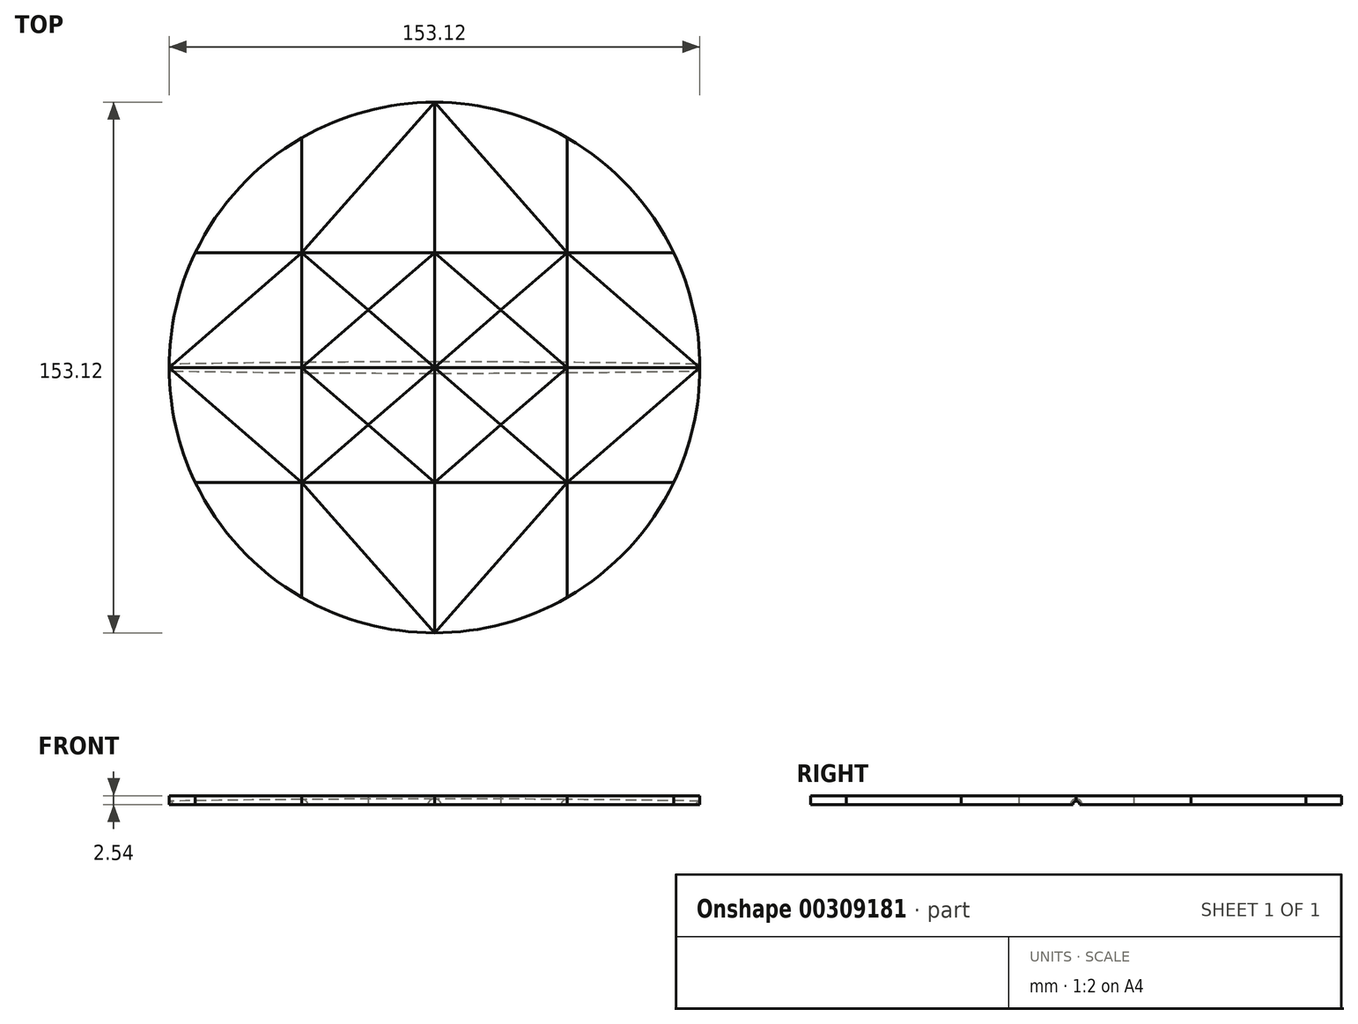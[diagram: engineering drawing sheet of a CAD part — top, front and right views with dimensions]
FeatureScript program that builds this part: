
annotation { "Feature Type Name" : "Feature", "Feature Type Description" : "" }
export const myFeature = defineFeature(function(context is Context, id is Id, definition is map)
    precondition{}
    {
        {
            var Q0;
            Q0=qCreatedBy(makeId("Top.planeOp"),FACE);
            var sketch = newSketch(context, id + "F0", { "sketchPlane" : qUnion([Q0])});
            skCircle(sketch, "E0", {"center": v(0, 0) * mm, "radius": 76.56 * mm});
            skLineSegment(sketch, "E1", {"start": v(0, 0) * mm, "end": v(-76.56, 0) * mm});
            skLineSegment(sketch, "E2", {"start": v(0, 0) * mm, "end": v(0, 76.56) * mm});
            skLineSegment(sketch, "E3", {"start": v(0, 0) * mm, "end": v(76.56, 0) * mm});
            skLineSegment(sketch, "E4", {"start": v(0, 0) * mm, "end": v(0, -76.56) * mm});
            skLineSegment(sketch, "E5", {"start": v(-38.28, 0) * mm, "end": v(-38.28, 66.3) * mm});
            skLineSegment(sketch, "E6", {"start": v(-38.28, 0) * mm, "end": v(-38.28, -66.3) * mm});
            skLineSegment(sketch, "E7", {"start": v(38.28, 0) * mm, "end": v(38.28, 66.3) * mm});
            skLineSegment(sketch, "E8", {"start": v(38.28, 0) * mm, "end": v(38.28, -66.3) * mm});
            skLineSegment(sketch, "E9", {"start": v(-38.28, 33.15) * mm, "end": v(-69, 33.15) * mm});
            skLineSegment(sketch, "E10", {"start": v(-38.28, -33.15) * mm, "end": v(-69, -33.15) * mm});
            skLineSegment(sketch, "E11", {"start": v(38.28, 33.15) * mm, "end": v(69, 33.15) * mm});
            skLineSegment(sketch, "E12", {"start": v(38.28, -33.15) * mm, "end": v(69, -33.15) * mm});
            skLineSegment(sketch, "E13", {"start": v(38.28, -33.15) * mm, "end": v(0, -33.15) * mm});
            skPoint(sketch, "E13.endSnap0", {"position": v(0, -38.28) * mm});
            skLineSegment(sketch, "E14", {"start": v(0, -33.15) * mm, "end": v(-38.28, -33.15) * mm});
            skLineSegment(sketch, "E15", {"start": v(-38.28, 33.15) * mm, "end": v(0, 33.15) * mm});
            skLineSegment(sketch, "E16", {"start": v(0, 33.15) * mm, "end": v(38.28, 33.15) * mm});
            skLineSegment(sketch, "E17", {"start": v(0, 33.15) * mm, "end": v(-38.28, 0) * mm});
            skLineSegment(sketch, "E18", {"start": v(-38.28, 0) * mm, "end": v(0, -33.15) * mm});
            skLineSegment(sketch, "E19", {"start": v(0, -33.15) * mm, "end": v(38.28, 0) * mm});
            skLineSegment(sketch, "E20", {"start": v(38.28, 0) * mm, "end": v(0, 33.15) * mm});
            skLineSegment(sketch, "E21", {"start": v(38.28, 33.15) * mm, "end": v(76.56, 0) * mm});
            skLineSegment(sketch, "E22", {"start": v(76.56, 0) * mm, "end": v(38.28, -33.15) * mm});
            skLineSegment(sketch, "E23", {"start": v(-38.28, 33.15) * mm, "end": v(-76.56, 0) * mm});
            skLineSegment(sketch, "E24", {"start": v(-76.56, 0) * mm, "end": v(-38.28, -33.15) * mm});
            skLineSegment(sketch, "E25", {"start": v(-38.28, -33.15) * mm, "end": v(0, -76.56) * mm});
            skLineSegment(sketch, "E26", {"start": v(0, -76.56) * mm, "end": v(38.28, -33.15) * mm});
            skLineSegment(sketch, "E27", {"start": v(38.28, 33.15) * mm, "end": v(0, 76.56) * mm});
            skLineSegment(sketch, "E28", {"start": v(0, 76.56) * mm, "end": v(-38.28, 33.15) * mm});
            skLineSegment(sketch, "E29", {"start": v(-38.28, 33.15) * mm, "end": v(38.28, -33.15) * mm});
            skLineSegment(sketch, "E30", {"start": v(38.28, 33.15) * mm, "end": v(-38.28, -33.15) * mm});
            skSolve(sketch);
        }
        {
            var Q0;
            {var subQ0=sQuery(id+"F0.wireOp",EDGE,"E28");Q0=makeQuery(id+"F0.imprint","IMPRINT",FACE,{"disambiguationData":[TD([[makeQuery(id+"F0.imprint","IMPRINT",EDGE,{"derivedFrom":subQ0}),-1.0]])]});}
            extrude(context, id + "F1", {"entities" : qUnion([Q0]), "depth" : 2.54 * mm});
        }
        {
            var Q0;
            {var subQ3=sQuery(id+"F0.wireOp",EDGE,"E9");Q0=makeQuery(id+"F0.imprint","IMPRINT",FACE,{"disambiguationData":[TD([[makeQuery(id+"F0.imprint","IMPRINT",EDGE,{"derivedFrom":subQ3}),-1.0]])]});}
            extrude(context, id + "F2", {"entities" : qUnion([Q0]), "depth" : 2.54 * mm});
        }
        {
            var Q0;
            {var subQ2=sQuery(id+"F0.wireOp",EDGE,"E9");Q0=makeQuery(id+"F0.imprint","IMPRINT",FACE,{"disambiguationData":[TD([[makeQuery(id+"F0.imprint","IMPRINT",EDGE,{"derivedFrom":subQ2}),1.0]])]});}
            extrude(context, id + "F3", {"entities" : qUnion([Q0]), "depth" : 2.54 * mm});
        }
        {
            var Q0;
            {var subQ2=sQuery(id+"F0.wireOp",EDGE,"E10");Q0=makeQuery(id+"F0.imprint","IMPRINT",FACE,{"disambiguationData":[TD([[makeQuery(id+"F0.imprint","IMPRINT",EDGE,{"derivedFrom":subQ2}),-1.0]])]});}
            extrude(context, id + "F4", {"entities" : qUnion([Q0]), "depth" : 2.54 * mm});
        }
        {
            var Q0;
            {var subQ3=sQuery(id+"F0.wireOp",EDGE,"E10");Q0=makeQuery(id+"F0.imprint","IMPRINT",FACE,{"disambiguationData":[TD([[makeQuery(id+"F0.imprint","IMPRINT",EDGE,{"derivedFrom":subQ3}),1.0]])]});}
            extrude(context, id + "F5", {"entities" : qUnion([Q0]), "depth" : 2.54 * mm});
        }
        {
            var Q0;
            {var subQ0=sQuery(id+"F0.wireOp",EDGE,"E25");Q0=makeQuery(id+"F0.imprint","IMPRINT",FACE,{"disambiguationData":[TD([[makeQuery(id+"F0.imprint","IMPRINT",EDGE,{"derivedFrom":subQ0}),-1.0]])]});}
            extrude(context, id + "F6", {"entities" : qUnion([Q0]), "depth" : 2.54 * mm});
        }
        {
            var Q0;
            {var subQ0=sQuery(id+"F0.wireOp",EDGE,"E26");Q0=makeQuery(id+"F0.imprint","IMPRINT",FACE,{"disambiguationData":[TD([[makeQuery(id+"F0.imprint","IMPRINT",EDGE,{"derivedFrom":subQ0}),-1.0]])]});}
            extrude(context, id + "F7", {"entities" : qUnion([Q0]), "depth" : 2.54 * mm});
        }
        {
            var Q0;
            {var subQ3=sQuery(id+"F0.wireOp",EDGE,"E12");Q0=makeQuery(id+"F0.imprint","IMPRINT",FACE,{"disambiguationData":[TD([[makeQuery(id+"F0.imprint","IMPRINT",EDGE,{"derivedFrom":subQ3}),-1.0]])]});}
            extrude(context, id + "F8", {"entities" : qUnion([Q0]), "depth" : 2.54 * mm});
        }
        {
            var Q0;
            {var subQ2=sQuery(id+"F0.wireOp",EDGE,"E12");Q0=makeQuery(id+"F0.imprint","IMPRINT",FACE,{"disambiguationData":[TD([[makeQuery(id+"F0.imprint","IMPRINT",EDGE,{"derivedFrom":subQ2}),1.0]])]});}
            extrude(context, id + "F9", {"entities" : qUnion([Q0]), "depth" : 2.54 * mm});
        }
        {
            var Q0;
            {var subQ2=sQuery(id+"F0.wireOp",EDGE,"E11");Q0=makeQuery(id+"F0.imprint","IMPRINT",FACE,{"disambiguationData":[TD([[makeQuery(id+"F0.imprint","IMPRINT",EDGE,{"derivedFrom":subQ2}),-1.0]])]});}
            extrude(context, id + "F10", {"entities" : qUnion([Q0]), "depth" : 2.54 * mm});
        }
        {
            var Q0;
            {var subQ3=sQuery(id+"F0.wireOp",EDGE,"E11");Q0=makeQuery(id+"F0.imprint","IMPRINT",FACE,{"disambiguationData":[TD([[makeQuery(id+"F0.imprint","IMPRINT",EDGE,{"derivedFrom":subQ3}),1.0]])]});}
            extrude(context, id + "F11", {"entities" : qUnion([Q0]), "depth" : 2.54 * mm});
        }
        {
            var Q0;
            {var subQ0=sQuery(id+"F0.wireOp",EDGE,"E27");Q0=makeQuery(id+"F0.imprint","IMPRINT",FACE,{"disambiguationData":[TD([[makeQuery(id+"F0.imprint","IMPRINT",EDGE,{"derivedFrom":subQ0}),-1.0]])]});}
            extrude(context, id + "F12", {"entities" : qUnion([Q0]), "depth" : 2.54 * mm});
        }
        {
            var Q0;
            {var subQ2=sQuery(id+"F0.wireOp",EDGE,"E15");Q0=makeQuery(id+"F0.imprint","IMPRINT",FACE,{"disambiguationData":[TD([[makeQuery(id+"F0.imprint","IMPRINT",EDGE,{"derivedFrom":subQ2}),1.0]])]});}
            extrude(context, id + "F13", {"entities" : qUnion([Q0]), "depth" : 2.54 * mm});
        }
        {
            var Q0;
            {var subQ0=sQuery(id+"F0.wireOp",EDGE,"E15");Q0=makeQuery(id+"F0.imprint","IMPRINT",FACE,{"disambiguationData":[TD([[makeQuery(id+"F0.imprint","IMPRINT",EDGE,{"derivedFrom":subQ0}),-1.0]])]});}
            extrude(context, id + "F14", {"entities" : qUnion([Q0]), "depth" : 2.54 * mm});
        }
        {
            var Q0;
            {var subQ0=sQuery(id+"F0.wireOp",EDGE,"E17");var subQ3=sQuery(id+"F0.wireOp",EDGE,"E29");var subQ5=makeQuery(id+"F0.imprint","INTERSECT",VERTEX,{"derivedFrom":[subQ0,subQ3]});Q0=makeQuery(id+"F0.imprint","IMPRINT",FACE,{"disambiguationData":[TD([[makeQuery(id+"F0.imprint","IMPRINT",EDGE,{"disambiguationData":[TD([[subQ5,-1.0]])],"derivedFrom":subQ0}),-1.0]])]});}
            extrude(context, id + "F15", {"entities" : qUnion([Q0]), "depth" : 2.54 * mm});
        }
        {
            var Q0;
            {var subQ0=sQuery(id+"F0.wireOp",EDGE,"E23");Q0=makeQuery(id+"F0.imprint","IMPRINT",FACE,{"disambiguationData":[TD([[makeQuery(id+"F0.imprint","IMPRINT",EDGE,{"derivedFrom":subQ0}),1.0]])]});}
            extrude(context, id + "F16", {"entities" : qUnion([Q0]), "depth" : 2.54 * mm});
        }
        {
            var Q0;
            {var subQ0=sQuery(id+"F0.wireOp",EDGE,"E24");Q0=makeQuery(id+"F0.imprint","IMPRINT",FACE,{"disambiguationData":[TD([[makeQuery(id+"F0.imprint","IMPRINT",EDGE,{"derivedFrom":subQ0}),1.0]])]});}
            extrude(context, id + "F17", {"entities" : qUnion([Q0]), "depth" : 2.54 * mm});
        }
        {
            var Q0;
            {var subQ0=sQuery(id+"F0.wireOp",EDGE,"E18");var subQ3=sQuery(id+"F0.wireOp",EDGE,"E30");var subQ5=makeQuery(id+"F0.imprint","INTERSECT",VERTEX,{"derivedFrom":[subQ0,subQ3]});Q0=makeQuery(id+"F0.imprint","IMPRINT",FACE,{"disambiguationData":[TD([[makeQuery(id+"F0.imprint","IMPRINT",EDGE,{"disambiguationData":[TD([[subQ5,1.0]])],"derivedFrom":subQ0}),-1.0]])]});}
            extrude(context, id + "F18", {"entities" : qUnion([Q0]), "depth" : 2.54 * mm});
        }
        {
            var Q0;
            {var subQ0=sQuery(id+"F0.wireOp",EDGE,"E14");Q0=makeQuery(id+"F0.imprint","IMPRINT",FACE,{"disambiguationData":[TD([[makeQuery(id+"F0.imprint","IMPRINT",EDGE,{"derivedFrom":subQ0}),-1.0]])]});}
            extrude(context, id + "F19", {"entities" : qUnion([Q0]), "depth" : 2.54 * mm});
        }
        {
            var Q0;
            {var subQ2=sQuery(id+"F0.wireOp",EDGE,"E14");Q0=makeQuery(id+"F0.imprint","IMPRINT",FACE,{"disambiguationData":[TD([[makeQuery(id+"F0.imprint","IMPRINT",EDGE,{"derivedFrom":subQ2}),1.0]])]});}
            extrude(context, id + "F20", {"entities" : qUnion([Q0]), "depth" : 2.54 * mm});
        }
        {
            var Q0;
            {var subQ2=sQuery(id+"F0.wireOp",EDGE,"E13");Q0=makeQuery(id+"F0.imprint","IMPRINT",FACE,{"disambiguationData":[TD([[makeQuery(id+"F0.imprint","IMPRINT",EDGE,{"derivedFrom":subQ2}),1.0]])]});}
            extrude(context, id + "F21", {"entities" : qUnion([Q0]), "depth" : 2.54 * mm});
        }
        {
            var Q0;
            {var subQ0=sQuery(id+"F0.wireOp",EDGE,"E13");Q0=makeQuery(id+"F0.imprint","IMPRINT",FACE,{"disambiguationData":[TD([[makeQuery(id+"F0.imprint","IMPRINT",EDGE,{"derivedFrom":subQ0}),-1.0]])]});}
            extrude(context, id + "F22", {"entities" : qUnion([Q0]), "depth" : 2.54 * mm});
        }
        {
            var Q0;
            {var subQ0=sQuery(id+"F0.wireOp",EDGE,"E19");var subQ3=sQuery(id+"F0.wireOp",EDGE,"E29");var subQ5=makeQuery(id+"F0.imprint","INTERSECT",VERTEX,{"derivedFrom":[subQ0,subQ3]});Q0=makeQuery(id+"F0.imprint","IMPRINT",FACE,{"disambiguationData":[TD([[makeQuery(id+"F0.imprint","IMPRINT",EDGE,{"disambiguationData":[TD([[subQ5,-1.0]])],"derivedFrom":subQ0}),-1.0]])]});}
            extrude(context, id + "F23", {"entities" : qUnion([Q0]), "depth" : 2.54 * mm});
        }
        {
            var Q0;
            {var subQ0=sQuery(id+"F0.wireOp",EDGE,"E22");Q0=makeQuery(id+"F0.imprint","IMPRINT",FACE,{"disambiguationData":[TD([[makeQuery(id+"F0.imprint","IMPRINT",EDGE,{"derivedFrom":subQ0}),-1.0]])]});}
            extrude(context, id + "F24", {"entities" : qUnion([Q0]), "depth" : 2.54 * mm});
        }
        {
            var Q0;
            {var subQ0=sQuery(id+"F0.wireOp",EDGE,"E21");Q0=makeQuery(id+"F0.imprint","IMPRINT",FACE,{"disambiguationData":[TD([[makeQuery(id+"F0.imprint","IMPRINT",EDGE,{"derivedFrom":subQ0}),-1.0]])]});}
            extrude(context, id + "F25", {"entities" : qUnion([Q0]), "depth" : 2.54 * mm});
        }
        {
            var Q0;
            {var subQ0=sQuery(id+"F0.wireOp",EDGE,"E20");var subQ3=sQuery(id+"F0.wireOp",EDGE,"E30");var subQ5=makeQuery(id+"F0.imprint","INTERSECT",VERTEX,{"derivedFrom":[subQ0,subQ3]});Q0=makeQuery(id+"F0.imprint","IMPRINT",FACE,{"disambiguationData":[TD([[makeQuery(id+"F0.imprint","IMPRINT",EDGE,{"disambiguationData":[TD([[subQ5,1.0]])],"derivedFrom":subQ0}),-1.0]])]});}
            extrude(context, id + "F26", {"entities" : qUnion([Q0]), "depth" : 2.54 * mm});
        }
        {
            var Q0;
            {var subQ0=sQuery(id+"F0.wireOp",EDGE,"E16");Q0=makeQuery(id+"F0.imprint","IMPRINT",FACE,{"disambiguationData":[TD([[makeQuery(id+"F0.imprint","IMPRINT",EDGE,{"derivedFrom":subQ0}),-1.0]])]});}
            extrude(context, id + "F27", {"entities" : qUnion([Q0]), "depth" : 2.54 * mm});
        }
        {
            var Q0;
            {var subQ2=sQuery(id+"F0.wireOp",EDGE,"E16");Q0=makeQuery(id+"F0.imprint","IMPRINT",FACE,{"disambiguationData":[TD([[makeQuery(id+"F0.imprint","IMPRINT",EDGE,{"derivedFrom":subQ2}),1.0]])]});}
            extrude(context, id + "F28", {"entities" : qUnion([Q0]), "depth" : 2.54 * mm});
        }
        {
            var Q0;
            {var subQ0=sQuery(id+"F0.wireOp",EDGE,"E29");var subQ3=sQuery(id+"F0.wireOp",EDGE,"E17");var subQ5=makeQuery(id+"F0.imprint","INTERSECT",VERTEX,{"derivedFrom":[subQ3,subQ0]});Q0=makeQuery(id+"F0.imprint","IMPRINT",FACE,{"disambiguationData":[TD([[makeQuery(id+"F0.imprint","IMPRINT",EDGE,{"disambiguationData":[TD([[subQ5,1.0]])],"derivedFrom":subQ3}),1.0]])]});}
            extrude(context, id + "F29", {"entities" : qUnion([Q0]), "depth" : 2.54 * mm});
        }
        {
            var Q0;
            {var subQ0=sQuery(id+"F0.wireOp",EDGE,"E29");var subQ3=sQuery(id+"F0.wireOp",EDGE,"E17");var subQ5=makeQuery(id+"F0.imprint","INTERSECT",VERTEX,{"derivedFrom":[subQ3,subQ0]});Q0=makeQuery(id+"F0.imprint","IMPRINT",FACE,{"disambiguationData":[TD([[makeQuery(id+"F0.imprint","IMPRINT",EDGE,{"disambiguationData":[TD([[subQ5,-1.0]])],"derivedFrom":subQ3}),1.0]])]});}
            extrude(context, id + "F30", {"entities" : qUnion([Q0]), "depth" : 2.54 * mm});
        }
        {
            var Q0;
            {var subQ0=sQuery(id+"F0.wireOp",EDGE,"E30");var subQ3=sQuery(id+"F0.wireOp",EDGE,"E18");var subQ5=makeQuery(id+"F0.imprint","INTERSECT",VERTEX,{"derivedFrom":[subQ3,subQ0]});Q0=makeQuery(id+"F0.imprint","IMPRINT",FACE,{"disambiguationData":[TD([[makeQuery(id+"F0.imprint","IMPRINT",EDGE,{"disambiguationData":[TD([[subQ5,1.0]])],"derivedFrom":subQ3}),1.0]])]});}
            extrude(context, id + "F31", {"entities" : qUnion([Q0]), "depth" : 2.54 * mm});
        }
        {
            var Q0;
            {var subQ0=sQuery(id+"F0.wireOp",EDGE,"E30");var subQ3=sQuery(id+"F0.wireOp",EDGE,"E18");var subQ5=makeQuery(id+"F0.imprint","INTERSECT",VERTEX,{"derivedFrom":[subQ3,subQ0]});Q0=makeQuery(id+"F0.imprint","IMPRINT",FACE,{"disambiguationData":[TD([[makeQuery(id+"F0.imprint","IMPRINT",EDGE,{"disambiguationData":[TD([[subQ5,-1.0]])],"derivedFrom":subQ3}),1.0]])]});}
            extrude(context, id + "F32", {"entities" : qUnion([Q0]), "depth" : 2.54 * mm});
        }
        {
            var Q0;
            {var subQ0=sQuery(id+"F0.wireOp",EDGE,"E29");var subQ3=sQuery(id+"F0.wireOp",EDGE,"E19");var subQ5=makeQuery(id+"F0.imprint","INTERSECT",VERTEX,{"derivedFrom":[subQ3,subQ0]});Q0=makeQuery(id+"F0.imprint","IMPRINT",FACE,{"disambiguationData":[TD([[makeQuery(id+"F0.imprint","IMPRINT",EDGE,{"disambiguationData":[TD([[subQ5,1.0]])],"derivedFrom":subQ3}),1.0]])]});}
            extrude(context, id + "F33", {"entities" : qUnion([Q0]), "depth" : 2.54 * mm});
        }
        {
            var Q0;
            {var subQ0=sQuery(id+"F0.wireOp",EDGE,"E29");var subQ3=sQuery(id+"F0.wireOp",EDGE,"E19");var subQ5=makeQuery(id+"F0.imprint","INTERSECT",VERTEX,{"derivedFrom":[subQ3,subQ0]});Q0=makeQuery(id+"F0.imprint","IMPRINT",FACE,{"disambiguationData":[TD([[makeQuery(id+"F0.imprint","IMPRINT",EDGE,{"disambiguationData":[TD([[subQ5,-1.0]])],"derivedFrom":subQ3}),1.0]])]});}
            extrude(context, id + "F34", {"entities" : qUnion([Q0]), "depth" : 2.54 * mm});
        }
        {
            var Q0;
            {var subQ0=sQuery(id+"F0.wireOp",EDGE,"E30");var subQ3=sQuery(id+"F0.wireOp",EDGE,"E20");var subQ5=makeQuery(id+"F0.imprint","INTERSECT",VERTEX,{"derivedFrom":[subQ3,subQ0]});Q0=makeQuery(id+"F0.imprint","IMPRINT",FACE,{"disambiguationData":[TD([[makeQuery(id+"F0.imprint","IMPRINT",EDGE,{"disambiguationData":[TD([[subQ5,1.0]])],"derivedFrom":subQ3}),1.0]])]});}
            extrude(context, id + "F35", {"entities" : qUnion([Q0]), "depth" : 2.54 * mm});
        }
        {
            var Q0;
            {var subQ0=sQuery(id+"F0.wireOp",EDGE,"E30");var subQ3=sQuery(id+"F0.wireOp",EDGE,"E20");var subQ5=makeQuery(id+"F0.imprint","INTERSECT",VERTEX,{"derivedFrom":[subQ3,subQ0]});Q0=makeQuery(id+"F0.imprint","IMPRINT",FACE,{"disambiguationData":[TD([[makeQuery(id+"F0.imprint","IMPRINT",EDGE,{"disambiguationData":[TD([[subQ5,-1.0]])],"derivedFrom":subQ3}),1.0]])]});}
            extrude(context, id + "F36", {"entities" : qUnion([Q0]), "depth" : 2.54 * mm});
        }
        {
            var Q0;
            Q0=qCreatedBy(makeId("Front.planeOp"),FACE);
            var sketch = newSketch(context, id + "F37", { "sketchPlane" : qUnion([Q0])});
            skLineSegment(sketch, "E31", {"start": v(-120.06, 0) * mm, "end": v(120.02, 0) * mm});
            skArc(sketch, "E32", {"start": v(120.02, 0) * mm, "mid": v(-0.02, 1.64) * mm, "end": v(-120.06, 0) * mm});
            skSolve(sketch);
        }
        {
            var Q0;
            Q0 = qSketchRegion(id + "F37", true);
            var Q1;
            Q1=sQuery(id+"F37.wireOp",EDGE,"E31");
            revolve(context, id + "F38", {"operationType" : NewBodyOperationType.REMOVE, "entities" : qUnion([Q0]), "axis" : qUnion([Q1]), "revolveType" : RevolveType.FULL, "oppositeDirection" : true});
        }
    });
